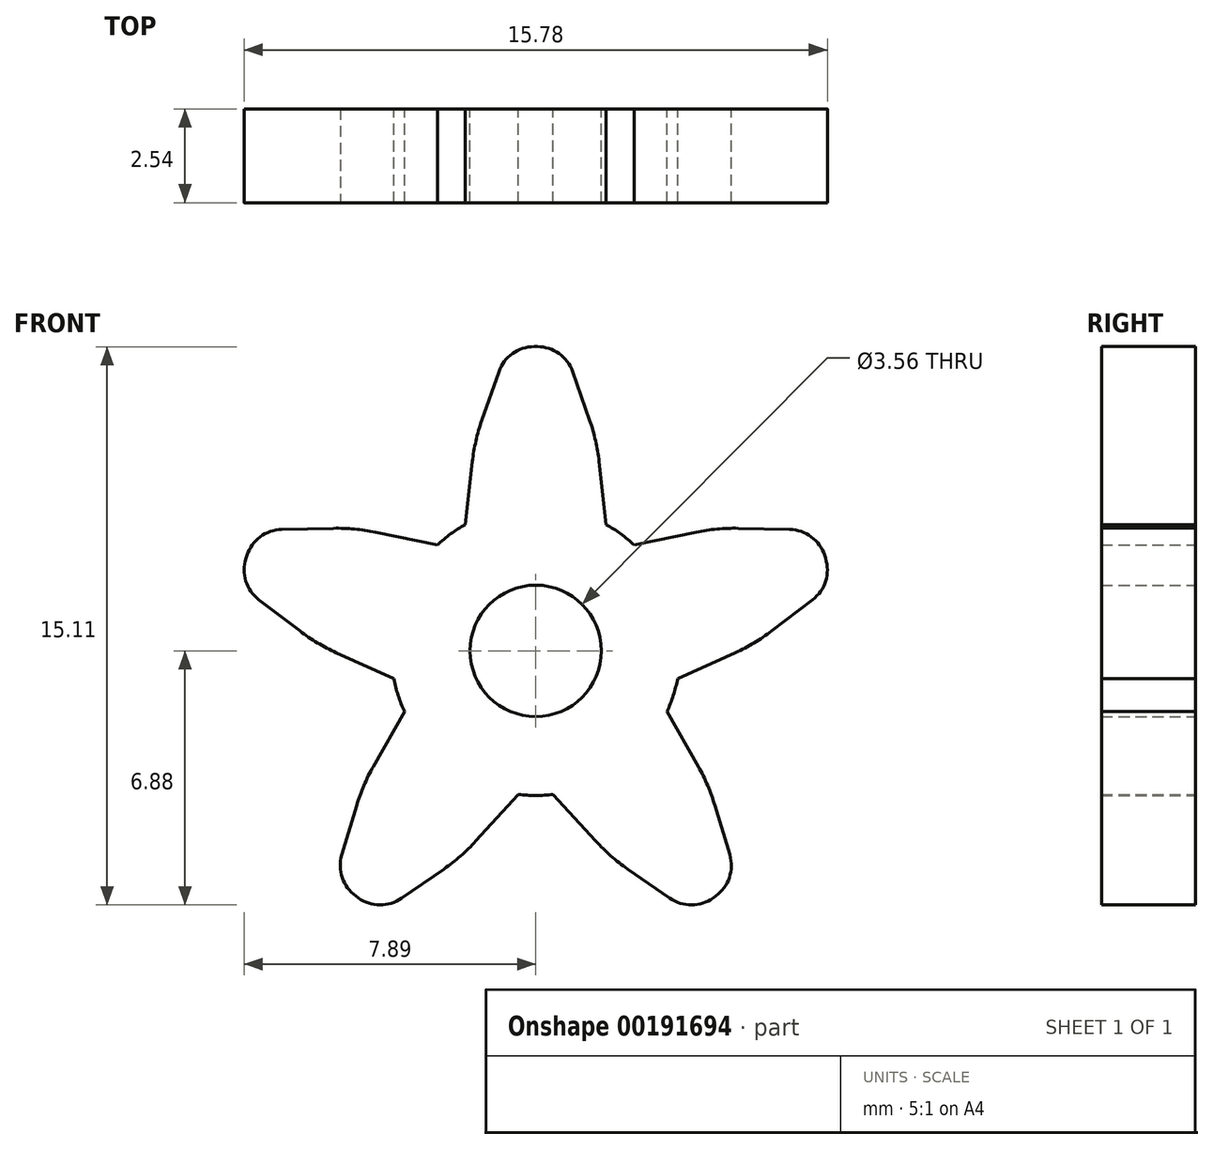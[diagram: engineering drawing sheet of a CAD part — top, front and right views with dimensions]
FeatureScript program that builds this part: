
annotation { "Feature Type Name" : "Feature", "Feature Type Description" : "" }
export const myFeature = defineFeature(function(context is Context, id is Id, definition is map)
    precondition{}
    {
        {
            var Q0;
            Q0=qCreatedBy(makeId("Front.planeOp"),FACE);
            var sketch = newSketch(context, id + "F0", { "sketchPlane" : qUnion([Q0])});
            skLineSegment(sketch, "E0", {"start": v(-1.9, 7.38) * mm, "end": v(-0.76, 12.2) * mm, "construction": true});
            skLineSegment(sketch, "E1", {"start": v(-0.76, 12.2) * mm, "end": v(0.76, 12.2) * mm});
            skLineSegment(sketch, "E2", {"start": v(0.76, 12.2) * mm, "end": v(1.9, 7.38) * mm, "construction": true});
            skLineSegment(sketch, "E3", {"start": v(-1.9, 7.38) * mm, "end": v(-1.65, 9.65) * mm});
            skPoint(sketch, "E3.endSnap0", {"position": v(-1.33, 9.79) * mm});
            skLineSegment(sketch, "E4", {"start": v(-1.65, 9.65) * mm, "end": v(-0.76, 12.2) * mm});
            skLineSegment(sketch, "E5", {"start": v(1.9, 7.38) * mm, "end": v(1.65, 9.65) * mm});
            skPoint(sketch, "E5.endSnap0", {"position": v(1.33, 9.79) * mm});
            skLineSegment(sketch, "E6", {"start": v(1.65, 9.65) * mm, "end": v(0.76, 12.2) * mm});
            skLineSegment(sketch, "E7.1.0", {"start": v(-8.07, 5.78) * mm, "end": v(-7.6, 7.23) * mm});
            skLineSegment(sketch, "E7.1.1", {"start": v(-4.9, 7.29) * mm, "end": v(-7.6, 7.23) * mm});
            skLineSegment(sketch, "E7.1.2", {"start": v(-2.66, 6.83) * mm, "end": v(-4.9, 7.29) * mm});
            skLineSegment(sketch, "E7.1.3", {"start": v(-5.92, 4.15) * mm, "end": v(-8.07, 5.78) * mm});
            skLineSegment(sketch, "E7.1.4", {"start": v(-3.84, 3.2) * mm, "end": v(-5.92, 4.15) * mm});
            skLineSegment(sketch, "E7.2.0", {"start": v(-4.22, -3.15) * mm, "end": v(-5.46, -2.25) * mm});
            skLineSegment(sketch, "E7.2.1", {"start": v(-4.68, 0.32) * mm, "end": v(-5.46, -2.25) * mm});
            skLineSegment(sketch, "E7.2.2", {"start": v(-3.55, 2.31) * mm, "end": v(-4.68, 0.32) * mm});
            skLineSegment(sketch, "E7.2.3", {"start": v(-2.01, -1.62) * mm, "end": v(-4.22, -3.15) * mm});
            skLineSegment(sketch, "E7.2.4", {"start": v(-0.47, 0.07) * mm, "end": v(-2.01, -1.62) * mm});
            skLineSegment(sketch, "E7.3.0", {"start": v(5.46, -2.25) * mm, "end": v(4.22, -3.15) * mm});
            skLineSegment(sketch, "E7.3.1", {"start": v(2.01, -1.62) * mm, "end": v(4.22, -3.15) * mm});
            skLineSegment(sketch, "E7.3.2", {"start": v(0.47, 0.07) * mm, "end": v(2.01, -1.62) * mm});
            skLineSegment(sketch, "E7.3.3", {"start": v(4.68, 0.32) * mm, "end": v(5.46, -2.25) * mm});
            skLineSegment(sketch, "E7.3.4", {"start": v(3.55, 2.31) * mm, "end": v(4.68, 0.32) * mm});
            skLineSegment(sketch, "E7.4.0", {"start": v(7.6, 7.23) * mm, "end": v(8.07, 5.78) * mm});
            skLineSegment(sketch, "E7.4.1", {"start": v(5.92, 4.15) * mm, "end": v(8.07, 5.78) * mm});
            skLineSegment(sketch, "E7.4.2", {"start": v(3.84, 3.2) * mm, "end": v(5.92, 4.15) * mm});
            skLineSegment(sketch, "E7.4.3", {"start": v(4.9, 7.29) * mm, "end": v(7.6, 7.23) * mm});
            skLineSegment(sketch, "E7.4.4", {"start": v(2.66, 6.83) * mm, "end": v(4.9, 7.29) * mm});
            skPoint(sketch, "E7.center", {"position": v(0, 3.96) * mm});
            skCircle(sketch, "E8", {"center": v(0, 3.96) * mm, "radius": 3.91 * mm});
            skCircle(sketch, "E9", {"center": v(0, 3.96) * mm, "radius": 1.78 * mm});
            skSolve(sketch);
        }
        {
            var Q0;
            Q0=qSketchRegion(id+"F0",true);
            extrude(context, id + "F1", {"entities" : qUnion([Q0]), "depth" : 2.54 * mm});
        }
        {
            var Q0;
            Q0=makeQuery(id+"F1.opExtrude","SWEPT_EDGE",EDGE,{"disambiguationData":[OSD([sQuery(id+"F0.wireOp",EDGE,"E7.9.1"),sQuery(id+"F0.wireOp",EDGE,"E7.9.2")])]});
            var Q1;
            Q1=makeQuery(id+"F1.opExtrude","SWEPT_EDGE",EDGE,{"disambiguationData":[OSD([sQuery(id+"F0.wireOp",EDGE,"E7.9.3"),sQuery(id+"F0.wireOp",EDGE,"E7.9.4")])]});
            var Q2;
            Q2=makeQuery(id+"F1.opExtrude","SWEPT_EDGE",EDGE,{"disambiguationData":[OSD([sQuery(id+"F0.wireOp",EDGE,"E5"),sQuery(id+"F0.wireOp",EDGE,"E6")])]});
            var Q3;
            Q3=makeQuery(id+"F1.opExtrude","SWEPT_EDGE",EDGE,{"disambiguationData":[OSD([sQuery(id+"F0.wireOp",EDGE,"E7.1.1"),sQuery(id+"F0.wireOp",EDGE,"E7.1.2")])]});
            var Q4;
            Q4=makeQuery(id+"F1.opExtrude","SWEPT_EDGE",EDGE,{"disambiguationData":[OSD([sQuery(id+"F0.wireOp",EDGE,"E7.2.1"),sQuery(id+"F0.wireOp",EDGE,"E7.2.2")])]});
            var Q5;
            Q5=makeQuery(id+"F1.opExtrude","SWEPT_EDGE",EDGE,{"disambiguationData":[OSD([sQuery(id+"F0.wireOp",EDGE,"E7.3.1"),sQuery(id+"F0.wireOp",EDGE,"E7.3.2")])]});
            var Q6;
            Q6=makeQuery(id+"F1.opExtrude","SWEPT_EDGE",EDGE,{"disambiguationData":[OSD([sQuery(id+"F0.wireOp",EDGE,"E7.4.1"),sQuery(id+"F0.wireOp",EDGE,"E7.4.2")])]});
            var Q7;
            Q7=makeQuery(id+"F1.opExtrude","SWEPT_EDGE",EDGE,{"disambiguationData":[OSD([sQuery(id+"F0.wireOp",EDGE,"E7.5.1"),sQuery(id+"F0.wireOp",EDGE,"E7.5.2")])]});
            var Q8;
            Q8=makeQuery(id+"F1.opExtrude","SWEPT_EDGE",EDGE,{"disambiguationData":[OSD([sQuery(id+"F0.wireOp",EDGE,"E7.6.1"),sQuery(id+"F0.wireOp",EDGE,"E7.6.2")])]});
            var Q9;
            Q9=makeQuery(id+"F1.opExtrude","SWEPT_EDGE",EDGE,{"disambiguationData":[OSD([sQuery(id+"F0.wireOp",EDGE,"E7.7.1"),sQuery(id+"F0.wireOp",EDGE,"E7.7.2")])]});
            var Q10;
            Q10=makeQuery(id+"F1.opExtrude","SWEPT_EDGE",EDGE,{"disambiguationData":[OSD([sQuery(id+"F0.wireOp",EDGE,"E7.8.1"),sQuery(id+"F0.wireOp",EDGE,"E7.8.2")])]});
            var Q11;
            Q11=makeQuery(id+"F1.opExtrude","SWEPT_EDGE",EDGE,{"disambiguationData":[OSD([sQuery(id+"F0.wireOp",EDGE,"E7.7.3"),sQuery(id+"F0.wireOp",EDGE,"E7.7.4")])]});
            var Q12;
            Q12=makeQuery(id+"F1.opExtrude","SWEPT_EDGE",EDGE,{"disambiguationData":[OSD([sQuery(id+"F0.wireOp",EDGE,"E7.8.3"),sQuery(id+"F0.wireOp",EDGE,"E7.8.4")])]});
            var Q13;
            Q13=makeQuery(id+"F1.opExtrude","SWEPT_EDGE",EDGE,{"disambiguationData":[OSD([sQuery(id+"F0.wireOp",EDGE,"E3"),sQuery(id+"F0.wireOp",EDGE,"E4")])]});
            var Q14;
            Q14=makeQuery(id+"F1.opExtrude","SWEPT_EDGE",EDGE,{"disambiguationData":[OSD([sQuery(id+"F0.wireOp",EDGE,"E7.1.3"),sQuery(id+"F0.wireOp",EDGE,"E7.1.4")])]});
            var Q15;
            Q15=makeQuery(id+"F1.opExtrude","SWEPT_EDGE",EDGE,{"disambiguationData":[OSD([sQuery(id+"F0.wireOp",EDGE,"E7.2.3"),sQuery(id+"F0.wireOp",EDGE,"E7.2.4")])]});
            var Q16;
            Q16=makeQuery(id+"F1.opExtrude","SWEPT_EDGE",EDGE,{"disambiguationData":[OSD([sQuery(id+"F0.wireOp",EDGE,"E7.3.3"),sQuery(id+"F0.wireOp",EDGE,"E7.3.4")])]});
            var Q17;
            Q17=makeQuery(id+"F1.opExtrude","SWEPT_EDGE",EDGE,{"disambiguationData":[OSD([sQuery(id+"F0.wireOp",EDGE,"E7.4.3"),sQuery(id+"F0.wireOp",EDGE,"E7.4.4")])]});
            var Q18;
            Q18=makeQuery(id+"F1.opExtrude","SWEPT_EDGE",EDGE,{"disambiguationData":[OSD([sQuery(id+"F0.wireOp",EDGE,"E7.5.3"),sQuery(id+"F0.wireOp",EDGE,"E7.5.4")])]});
            var Q19;
            Q19=makeQuery(id+"F1.opExtrude","SWEPT_EDGE",EDGE,{"disambiguationData":[OSD([sQuery(id+"F0.wireOp",EDGE,"E7.6.3"),sQuery(id+"F0.wireOp",EDGE,"E7.6.4")])]});
            fillet(context, id + "F2", {"entities" : qUnion([Q0, Q1, Q2, Q3, Q4, Q5, Q6, Q7, Q8, Q9, Q10, Q11, Q12, Q13, Q14, Q15, Q16, Q17, Q18, Q19]), "radius" : 5.08 * mm, "tangentPropagation" : true, "allowEdgeOverflow" : false});
        }
        {
            var Q0;
            Q0=makeQuery(id+"F1.opExtrude","SWEPT_EDGE",EDGE,{"disambiguationData":[OSD([sQuery(id+"F0.wireOp",EDGE,"E1"),sQuery(id+"F0.wireOp",EDGE,"E6")])]});
            var Q1;
            Q1=makeQuery(id+"F1.opExtrude","SWEPT_EDGE",EDGE,{"disambiguationData":[OSD([sQuery(id+"F0.wireOp",EDGE,"E1"),sQuery(id+"F0.wireOp",EDGE,"E4")])]});
            var Q2;
            Q2=makeQuery(id+"F1.opExtrude","SWEPT_EDGE",EDGE,{"disambiguationData":[OSD([sQuery(id+"F0.wireOp",EDGE,"E7.1.0"),sQuery(id+"F0.wireOp",EDGE,"E7.1.1")])]});
            var Q3;
            Q3=makeQuery(id+"F1.opExtrude","SWEPT_EDGE",EDGE,{"disambiguationData":[OSD([sQuery(id+"F0.wireOp",EDGE,"E7.1.0"),sQuery(id+"F0.wireOp",EDGE,"E7.1.3")])]});
            var Q4;
            Q4=makeQuery(id+"F1.opExtrude","SWEPT_EDGE",EDGE,{"disambiguationData":[OSD([sQuery(id+"F0.wireOp",EDGE,"E7.2.0"),sQuery(id+"F0.wireOp",EDGE,"E7.2.1")])]});
            var Q5;
            Q5=makeQuery(id+"F1.opExtrude","SWEPT_EDGE",EDGE,{"disambiguationData":[OSD([sQuery(id+"F0.wireOp",EDGE,"E7.9.0"),sQuery(id+"F0.wireOp",EDGE,"E7.9.3")])]});
            var Q6;
            Q6=makeQuery(id+"F1.opExtrude","SWEPT_EDGE",EDGE,{"disambiguationData":[OSD([sQuery(id+"F0.wireOp",EDGE,"E7.9.0"),sQuery(id+"F0.wireOp",EDGE,"E7.9.1")])]});
            var Q7;
            Q7=makeQuery(id+"F1.opExtrude","SWEPT_EDGE",EDGE,{"disambiguationData":[OSD([sQuery(id+"F0.wireOp",EDGE,"E7.8.0"),sQuery(id+"F0.wireOp",EDGE,"E7.8.3")])]});
            var Q8;
            Q8=makeQuery(id+"F1.opExtrude","SWEPT_EDGE",EDGE,{"disambiguationData":[OSD([sQuery(id+"F0.wireOp",EDGE,"E7.2.0"),sQuery(id+"F0.wireOp",EDGE,"E7.2.3")])]});
            var Q9;
            Q9=makeQuery(id+"F1.opExtrude","SWEPT_EDGE",EDGE,{"disambiguationData":[OSD([sQuery(id+"F0.wireOp",EDGE,"E7.3.0"),sQuery(id+"F0.wireOp",EDGE,"E7.3.1")])]});
            var Q10;
            Q10=makeQuery(id+"F1.opExtrude","SWEPT_EDGE",EDGE,{"disambiguationData":[OSD([sQuery(id+"F0.wireOp",EDGE,"E7.3.0"),sQuery(id+"F0.wireOp",EDGE,"E7.3.3")])]});
            var Q11;
            Q11=makeQuery(id+"F1.opExtrude","SWEPT_EDGE",EDGE,{"disambiguationData":[OSD([sQuery(id+"F0.wireOp",EDGE,"E7.4.0"),sQuery(id+"F0.wireOp",EDGE,"E7.4.1")])]});
            var Q12;
            Q12=makeQuery(id+"F1.opExtrude","SWEPT_EDGE",EDGE,{"disambiguationData":[OSD([sQuery(id+"F0.wireOp",EDGE,"E7.4.0"),sQuery(id+"F0.wireOp",EDGE,"E7.4.3")])]});
            var Q13;
            Q13=makeQuery(id+"F1.opExtrude","SWEPT_EDGE",EDGE,{"disambiguationData":[OSD([sQuery(id+"F0.wireOp",EDGE,"E7.5.0"),sQuery(id+"F0.wireOp",EDGE,"E7.5.1")])]});
            var Q14;
            Q14=makeQuery(id+"F1.opExtrude","SWEPT_EDGE",EDGE,{"disambiguationData":[OSD([sQuery(id+"F0.wireOp",EDGE,"E7.5.0"),sQuery(id+"F0.wireOp",EDGE,"E7.5.3")])]});
            var Q15;
            Q15=makeQuery(id+"F1.opExtrude","SWEPT_EDGE",EDGE,{"disambiguationData":[OSD([sQuery(id+"F0.wireOp",EDGE,"E7.6.0"),sQuery(id+"F0.wireOp",EDGE,"E7.6.1")])]});
            var Q16;
            Q16=makeQuery(id+"F1.opExtrude","SWEPT_EDGE",EDGE,{"disambiguationData":[OSD([sQuery(id+"F0.wireOp",EDGE,"E7.6.0"),sQuery(id+"F0.wireOp",EDGE,"E7.6.3")])]});
            var Q17;
            Q17=makeQuery(id+"F1.opExtrude","SWEPT_EDGE",EDGE,{"disambiguationData":[OSD([sQuery(id+"F0.wireOp",EDGE,"E7.7.0"),sQuery(id+"F0.wireOp",EDGE,"E7.7.3")])]});
            var Q18;
            Q18=makeQuery(id+"F1.opExtrude","SWEPT_EDGE",EDGE,{"disambiguationData":[OSD([sQuery(id+"F0.wireOp",EDGE,"E7.7.0"),sQuery(id+"F0.wireOp",EDGE,"E7.7.1")])]});
            var Q19;
            Q19=makeQuery(id+"F1.opExtrude","SWEPT_EDGE",EDGE,{"disambiguationData":[OSD([sQuery(id+"F0.wireOp",EDGE,"E7.8.0"),sQuery(id+"F0.wireOp",EDGE,"E7.8.1")])]});
            fillet(context, id + "F3", {"entities" : qUnion([Q0, Q1, Q2, Q3, Q4, Q5, Q6, Q7, Q8, Q9, Q10, Q11, Q12, Q13, Q14, Q15, Q16, Q17, Q18, Q19]), "radius" : 1.02 * mm, "tangentPropagation" : true, "allowEdgeOverflow" : false});
        }
    });
